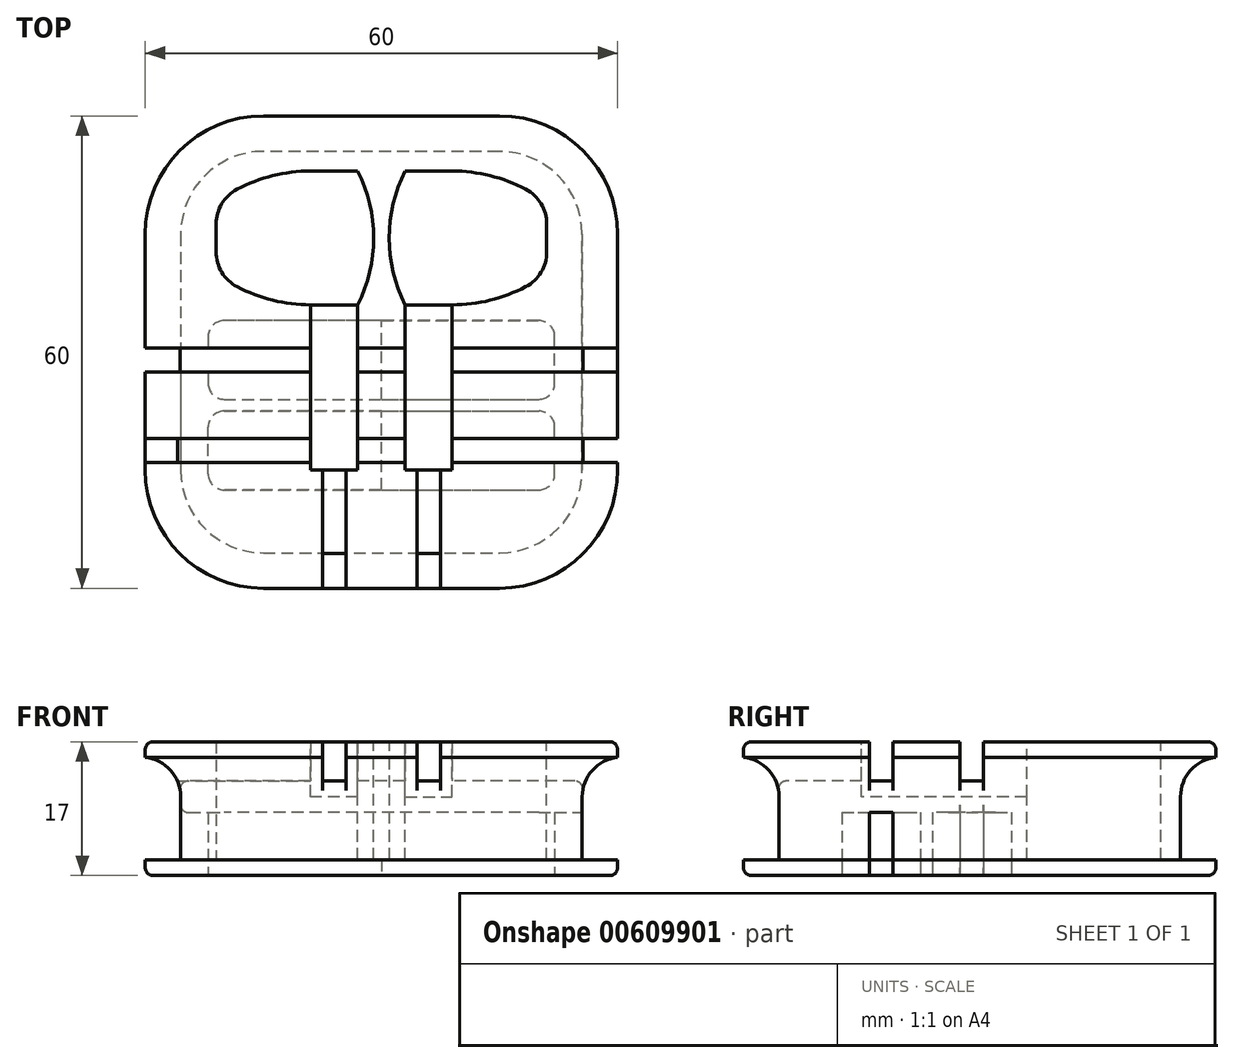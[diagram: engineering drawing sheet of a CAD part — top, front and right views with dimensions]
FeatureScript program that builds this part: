
annotation { "Feature Type Name" : "Feature", "Feature Type Description" : "" }
export const myFeature = defineFeature(function(context is Context, id is Id, definition is map)
    precondition{}
    {
        {
            var Q0;
            Q0=qCreatedBy(makeId("Top.planeOp"),FACE);
            var sketch = newSketch(context, id + "F0", { "sketchPlane" : qUnion([Q0])});
            skLineSegment(sketch, "E0.bottom", {"start": v(-30, 30) * mm, "end": v(30, 30) * mm});
            skLineSegment(sketch, "E0.top", {"start": v(-30, -30) * mm, "end": v(30, -30) * mm});
            skLineSegment(sketch, "E0.left", {"start": v(-30, 30) * mm, "end": v(-30, -30) * mm});
            skLineSegment(sketch, "E0.right", {"start": v(30, 30) * mm, "end": v(30, -30) * mm});
            skSolve(sketch);
        }
        {
            var Q0;
            Q0 = qSketchRegion(id + "F0", true);
            extrude(context, id + "F1", {"entities" : qUnion([Q0]), "endBound" : BoundingType.SYMMETRIC, "depth" : 17 * mm, "offsetDistance" : 25 * mm});
        }
        {
            var Q0;
            Q0=makeQuery(id+"F1.opExtrude","SWEPT_EDGE",EDGE,{"disambiguationData":[OSD([sQuery(id+"F0.wireOp",EDGE,"E0.bottom"),sQuery(id+"F0.wireOp",EDGE,"E0.left")])]});
            var Q1;
            Q1=makeQuery(id+"F1.opExtrude","SWEPT_EDGE",EDGE,{"disambiguationData":[OSD([sQuery(id+"F0.wireOp",EDGE,"E0.top"),sQuery(id+"F0.wireOp",EDGE,"E0.left")])]});
            var Q2;
            Q2=makeQuery(id+"F1.opExtrude","SWEPT_EDGE",EDGE,{"disambiguationData":[OSD([sQuery(id+"F0.wireOp",EDGE,"E0.bottom"),sQuery(id+"F0.wireOp",EDGE,"E0.right")])]});
            var Q3;
            Q3=makeQuery(id+"F1.opExtrude","SWEPT_EDGE",EDGE,{"disambiguationData":[OSD([sQuery(id+"F0.wireOp",EDGE,"E0.top"),sQuery(id+"F0.wireOp",EDGE,"E0.right")])]});
            fillet(context, id + "F2", {"entities" : qUnion([Q0, Q1, Q2, Q3]), "radius" : 15 * mm, "tangentPropagation" : true, "allowEdgeOverflow" : false});
        }
        {
            var Q0;
            Q0=makeQuery(id+"F1.opExtrude","CAP_FACE",FACE,{"disambiguationData":[OSD([sQuery(id+"F0.wireOp",EDGE,"E0.bottom"),sQuery(id+"F0.wireOp",EDGE,"E0.top"),sQuery(id+"F0.wireOp",EDGE,"E0.left"),sQuery(id+"F0.wireOp",EDGE,"E0.right")])],"isStart":false});
            cPlane(context, id + "F3", {"entities" : qUnion([Q0]), "cplaneType" : CPlaneType.OFFSET, "offset" : 2 * mm, "oppositeDirection" : true, "width" : 150 * mm, "height" : 150 * mm});
        }
        {
            var Q0;
            Q0=makeQuery(id+"F1.opExtrude","CAP_FACE",FACE,{"disambiguationData":[OSD([sQuery(id+"F0.wireOp",EDGE,"E0.bottom"),sQuery(id+"F0.wireOp",EDGE,"E0.top"),sQuery(id+"F0.wireOp",EDGE,"E0.left"),sQuery(id+"F0.wireOp",EDGE,"E0.right")])],"isStart":true});
            cPlane(context, id + "F4", {"entities" : qUnion([Q0]), "cplaneType" : CPlaneType.OFFSET, "offset" : 2 * mm, "oppositeDirection" : true, "width" : 150 * mm, "height" : 150 * mm});
        }
        {
            var Q0;
            Q0=qCreatedBy(id+"F3.planeOp",FACE);
            var sketch = newSketch(context, id + "F5", { "sketchPlane" : qUnion([Q0])});
            skLineSegment(sketch, "E1.0", {"start": v(-15, 25.5) * mm, "end": v(15, 25.5) * mm});
            skArc(sketch, "E1.1", {"start": v(25.5, 15) * mm, "mid": v(22.42, 22.42) * mm, "end": v(15, 25.5) * mm});
            skArc(sketch, "E1.2", {"start": v(-15, 25.5) * mm, "mid": v(-22.42, 22.42) * mm, "end": v(-25.5, 15) * mm});
            skLineSegment(sketch, "E1.3", {"start": v(25.5, 15) * mm, "end": v(25.5, -15) * mm});
            skLineSegment(sketch, "E1.4", {"start": v(-25.5, 15) * mm, "end": v(-25.5, -15) * mm});
            skArc(sketch, "E1.5", {"start": v(-25.5, -15) * mm, "mid": v(-22.42, -22.42) * mm, "end": v(-15, -25.5) * mm});
            skLineSegment(sketch, "E1.6", {"start": v(-15, -25.5) * mm, "end": v(15, -25.5) * mm});
            skArc(sketch, "E1.7", {"start": v(15, -25.5) * mm, "mid": v(22.42, -22.42) * mm, "end": v(25.5, -15) * mm});
            skLineSegment(sketch, "E2.0", {"start": v(-15, 30) * mm, "end": v(15, 30) * mm});
            skArc(sketch, "E3.0", {"start": v(-15, 30) * mm, "mid": v(-25.6, 25.6) * mm, "end": v(-30, 15) * mm});
            skLineSegment(sketch, "E4.0", {"start": v(-30, 15) * mm, "end": v(-30, -15) * mm});
            skArc(sketch, "E5.0", {"start": v(-30, -15) * mm, "mid": v(-25.6, -25.6) * mm, "end": v(-15, -30) * mm});
            skLineSegment(sketch, "E6.0", {"start": v(-15, -30) * mm, "end": v(15, -30) * mm});
            skArc(sketch, "E7.0", {"start": v(30, 15) * mm, "mid": v(25.6, 25.6) * mm, "end": v(15, 30) * mm});
            skLineSegment(sketch, "E8.0", {"start": v(30, 15) * mm, "end": v(30, -15) * mm});
            skArc(sketch, "E9.0", {"start": v(15, -30) * mm, "mid": v(25.6, -25.6) * mm, "end": v(30, -15) * mm});
            skSolve(sketch);
        }
        {
            var Q0;
            Q0 = qSketchRegion(id + "F5", true);
            var Q1;
            Q1=qCreatedBy(id+"F4.planeOp",FACE);
            extrude(context, id + "F6", {"entities" : qUnion([Q0]), "operationType" : NewBodyOperationType.REMOVE, "endBound" : BoundingType.UP_TO_SURFACE, "oppositeDirection" : true, "depth" : 25 * mm, "endBoundEntityFace" : qUnion([Q1]), "offsetDistance" : 25 * mm});
        }
        {
            var Q0;
            Q0=makeQuery(id+"F6.boolean.opBoolean","COPY",EDGE,{"derivedFrom":makeQuery(id+"F6.opExtrude","TWEAK_EDGE",EDGE,{"derivedFrom":[dummyQuery(id+"F4.planeOp",FACE),makeQuery(id+"F5.imprint","IMPRINT",EDGE,{"derivedFrom":sQuery(id+"F5.wireOp",EDGE,"E1.0")})]})});
            var Q1;
            Q1=makeQuery(id+"F6.boolean.opBoolean","COPY",EDGE,{"derivedFrom":makeQuery(id+"F6.opExtrude","CAP_EDGE",EDGE,{"disambiguationData":[OSD([sQuery(id+"F5.wireOp",EDGE,"E1.0")])],"isStart":true})});
            fillet(context, id + "F7", {"entities" : qUnion([Q0, Q1]), "radius" : 5 * mm, "tangentPropagation" : true, "allowEdgeOverflow" : false});
        }
        {
            var Q0;
            Q0=makeQuery(id+"F1.opExtrude","CAP_FACE",FACE,{"disambiguationData":[OSD([sQuery(id+"F0.wireOp",EDGE,"E0.bottom"),sQuery(id+"F0.wireOp",EDGE,"E0.top"),sQuery(id+"F0.wireOp",EDGE,"E0.left"),sQuery(id+"F0.wireOp",EDGE,"E0.right")])],"isStart":false});
            var sketch = newSketch(context, id + "F8", { "sketchPlane" : qUnion([Q0])});
            skLineSegment(sketch, "E10.bottom", {"start": v(3, 23) * mm, "end": v(9, 23) * mm});
            skLineSegment(sketch, "E10.top", {"start": v(3, -15) * mm, "end": v(9, -15) * mm});
            skLineSegment(sketch, "E10.left", {"start": v(3, 23) * mm, "end": v(3, -15) * mm});
            skLineSegment(sketch, "E10.right", {"start": v(9, 23) * mm, "end": v(9, -15) * mm});
            skLineSegment(sketch, "E11.MirrorCS", {"start": v(-9, 23) * mm, "end": v(-9, -15) * mm});
            skLineSegment(sketch, "E12.MirrorCS", {"start": v(-3, 23) * mm, "end": v(-3, -15) * mm});
            skLineSegment(sketch, "E13.MirrorCS", {"start": v(-3, -15) * mm, "end": v(-9, -15) * mm});
            skLineSegment(sketch, "E14.MirrorCS", {"start": v(-3, 23) * mm, "end": v(-9, 23) * mm});
            skSolve(sketch);
        }
        {
            var Q0;
            Q0 = qSketchRegion(id + "F8", true);
            extrude(context, id + "F9", {"entities" : qUnion([Q0]), "operationType" : NewBodyOperationType.REMOVE, "oppositeDirection" : true, "depth" : 7 * mm, "offsetDistance" : 25 * mm});
        }
        {
            var Q0;
            Q0=makeQuery(id+"F1.opExtrude","CAP_FACE",FACE,{"disambiguationData":[OSD([sQuery(id+"F0.wireOp",EDGE,"E0.bottom"),sQuery(id+"F0.wireOp",EDGE,"E0.top"),sQuery(id+"F0.wireOp",EDGE,"E0.left"),sQuery(id+"F0.wireOp",EDGE,"E0.right")])],"isStart":false});
            var sketch = newSketch(context, id + "F10", { "sketchPlane" : qUnion([Q0])});
            skLineSegment(sketch, "E15.0", {"start": v(3, 23) * mm, "end": v(9, 23) * mm});
            skLineSegment(sketch, "E16", {"start": v(3, 6) * mm, "end": v(9, 6) * mm});
            skArc(sketch, "E17", {"start": v(3, 23) * mm, "mid": v(1, 14.5) * mm, "end": v(3, 6) * mm});
            skLineSegment(sketch, "E18", {"start": v(21, 19) * mm, "end": v(21, 10) * mm});
            skArc(sketch, "E19", {"start": v(21, 19) * mm, "mid": v(15.32, 21.97) * mm, "end": v(9, 23) * mm});
            skArc(sketch, "E20", {"start": v(9, 6) * mm, "mid": v(15.32, 7.03) * mm, "end": v(21, 10) * mm});
            skLineSegment(sketch, "E21.MirrorCS", {"start": v(-21, 19) * mm, "end": v(-21, 10) * mm});
            skArc(sketch, "E22.MirrorCS", {"start": v(-9, 6) * mm, "mid": v(-15.32, 7.03) * mm, "end": v(-21, 10) * mm});
            skArc(sketch, "E23.MirrorCS", {"start": v(-21, 19) * mm, "mid": v(-15.32, 21.97) * mm, "end": v(-9, 23) * mm});
            skArc(sketch, "E24.MirrorCS", {"start": v(-3, 23) * mm, "mid": v(-1, 14.5) * mm, "end": v(-3, 6) * mm});
            skLineSegment(sketch, "E25.MirrorCS", {"start": v(-3, 23) * mm, "end": v(-9, 23) * mm});
            skLineSegment(sketch, "E26.MirrorCS", {"start": v(-3, 6) * mm, "end": v(-9, 6) * mm});
            skSolve(sketch);
        }
        {
            var Q0;
            Q0 = qSketchRegion(id + "F10", true);
            var Q1;
            Q1=qCreatedBy(id+"F4.planeOp",FACE);
            extrude(context, id + "F11", {"entities" : qUnion([Q0]), "operationType" : NewBodyOperationType.REMOVE, "endBound" : BoundingType.UP_TO_SURFACE, "oppositeDirection" : true, "depth" : 18 * mm, "endBoundEntityFace" : qUnion([Q1]), "offsetDistance" : 25 * mm});
        }
        {
            var Q0;
            Q0=makeQuery(id+"F1.opExtrude","CAP_FACE",FACE,{"disambiguationData":[OSD([sQuery(id+"F0.wireOp",EDGE,"E0.bottom"),sQuery(id+"F0.wireOp",EDGE,"E0.top"),sQuery(id+"F0.wireOp",EDGE,"E0.left"),sQuery(id+"F0.wireOp",EDGE,"E0.right")])],"isStart":false});
            var sketch = newSketch(context, id + "F12", { "sketchPlane" : qUnion([Q0])});
            skLineSegment(sketch, "E27.0", {"start": v(-7.5, -30) * mm, "end": v(-4.5, -30) * mm});
            skLineSegment(sketch, "E28.0", {"start": v(-4.5, -15) * mm, "end": v(-7.5, -15) * mm});
            skLineSegment(sketch, "E29", {"start": v(-6, -15) * mm, "end": v(-6, -30) * mm, "construction": true});
            skLineSegment(sketch, "E30", {"start": v(-7.5, -15) * mm, "end": v(-7.5, -30) * mm});
            skLineSegment(sketch, "E31", {"start": v(-4.5, -15) * mm, "end": v(-4.5, -30) * mm});
            skPoint(sketch, "E32.orphan", {"position": v(-3, -15) * mm});
            skPoint(sketch, "E33.orphan", {"position": v(-9, -15) * mm});
            skPoint(sketch, "E34.orphan", {"position": v(-15, -30) * mm});
            skLineSegment(sketch, "E35.MirrorCS", {"start": v(7.5, -30) * mm, "end": v(4.5, -30) * mm});
            skLineSegment(sketch, "E36.MirrorCS", {"start": v(4.5, -15) * mm, "end": v(7.5, -15) * mm});
            skPoint(sketch, "E37.MirrorP", {"position": v(9, -15) * mm});
            skPoint(sketch, "E38.MirrorP", {"position": v(3, -15) * mm});
            skLineSegment(sketch, "E39.MirrorCS", {"start": v(6, -15) * mm, "end": v(6, -30) * mm, "construction": true});
            skLineSegment(sketch, "E40.MirrorCS", {"start": v(7.5, -15) * mm, "end": v(7.5, -30) * mm});
            skLineSegment(sketch, "E41.MirrorCS", {"start": v(4.5, -15) * mm, "end": v(4.5, -30) * mm});
            skLineSegment(sketch, "E42.top", {"start": v(30, -2.5) * mm, "end": v(-30, -2.5) * mm});
            skLineSegment(sketch, "E42.left", {"start": v(30, 0.5) * mm, "end": v(30, -2.5) * mm});
            skLineSegment(sketch, "E42.right", {"start": v(-30, 0.5) * mm, "end": v(-30, -2.5) * mm});
            skLineSegment(sketch, "E43", {"start": v(-30, 0.5) * mm, "end": v(30, 0.5) * mm});
            skPoint(sketch, "E44.orphan", {"position": v(30, 0) * mm});
            skSolve(sketch);
        }
        {
            var Q0;
            Q0 = qSketchRegion(id + "F12", true);
            extrude(context, id + "F13", {"entities" : qUnion([Q0]), "operationType" : NewBodyOperationType.REMOVE, "oppositeDirection" : true, "depth" : 5 * mm, "offsetDistance" : 25 * mm});
        }
        {
            var Q0;
            Q0=makeQuery(id+"F1.opExtrude","CAP_FACE",FACE,{"disambiguationData":[OSD([sQuery(id+"F0.wireOp",EDGE,"E0.bottom"),sQuery(id+"F0.wireOp",EDGE,"E0.top"),sQuery(id+"F0.wireOp",EDGE,"E0.left"),sQuery(id+"F0.wireOp",EDGE,"E0.right")])],"isStart":true});
            var sketch = newSketch(context, id + "F14", { "sketchPlane" : qUnion([Q0])});
            skLineSegment(sketch, "E45.bottom", {"start": v(-30, -0.5) * mm, "end": v(-22, -0.5) * mm});
            skLineSegment(sketch, "E45.top", {"start": v(-30, 2.5) * mm, "end": v(-22, 2.5) * mm});
            skLineSegment(sketch, "E45.left", {"start": v(-30, -0.5) * mm, "end": v(-30, 2.5) * mm});
            skLineSegment(sketch, "E46", {"start": v(-30, 1) * mm, "end": v(30, 1) * mm, "construction": true});
            skLineSegment(sketch, "E47", {"start": v(-22, 2.5) * mm, "end": v(-22, 6) * mm});
            skLineSegment(sketch, "E48", {"start": v(-22, 6) * mm, "end": v(0, 6) * mm});
            skLineSegment(sketch, "E49", {"start": v(0, 6) * mm, "end": v(0, -4) * mm});
            skLineSegment(sketch, "E50", {"start": v(0, -4) * mm, "end": v(-22, -4) * mm});
            skLineSegment(sketch, "E51", {"start": v(-22, -4) * mm, "end": v(-22, -0.5) * mm});
            skLineSegment(sketch, "E52.bottom", {"start": v(0, 17.5) * mm, "end": v(22, 17.5) * mm});
            skLineSegment(sketch, "E52.top", {"start": v(0, 7.5) * mm, "end": v(22, 7.5) * mm});
            skLineSegment(sketch, "E52.left", {"start": v(0, 17.5) * mm, "end": v(0, 7.5) * mm});
            skLineSegment(sketch, "E52.right", {"start": v(22, 17.5) * mm, "end": v(22, 14) * mm});
            skLineSegment(sketch, "E53", {"start": v(0, 12.5) * mm, "end": v(29.8, 12.5) * mm, "construction": true});
            skPoint(sketch, "E54.orphan", {"position": v(15, 30) * mm});
            skPoint(sketch, "E55.orphan", {"position": v(30, 15) * mm});
            skLineSegment(sketch, "E56.trimOffspring", {"start": v(22, 11) * mm, "end": v(22, 7.5) * mm});
            skLineSegment(sketch, "E57", {"start": v(22, 11) * mm, "end": v(30, 11) * mm});
            skLineSegment(sketch, "E58", {"start": v(22, 14) * mm, "end": v(30, 14) * mm});
            skLineSegment(sketch, "E59.trimOffspring", {"start": v(30, 11) * mm, "end": v(30, 14) * mm});
            skSolve(sketch);
        }
        {
            var Q0;
            Q0 = qSketchRegion(id + "F14", true);
            extrude(context, id + "F15", {"entities" : qUnion([Q0]), "operationType" : NewBodyOperationType.REMOVE, "oppositeDirection" : true, "depth" : 8 * mm, "offsetDistance" : 25 * mm});
        }
        {
            var Q0;
            Q0=qCreatedBy(id+"F4.planeOp",FACE);
            var sketch = newSketch(context, id + "F16", { "sketchPlane" : qUnion([Q0])});
            skPoint(sketch, "E60.0", {"position": v(0, 6) * mm});
            skPoint(sketch, "E61.0", {"position": v(0, -4) * mm});
            skLineSegment(sketch, "E62.bottom", {"start": v(0, 6) * mm, "end": v(22, 6) * mm});
            skLineSegment(sketch, "E62.top", {"start": v(0, -4) * mm, "end": v(22, -4) * mm});
            skLineSegment(sketch, "E62.left", {"start": v(0, 6) * mm, "end": v(0, -4) * mm});
            skLineSegment(sketch, "E62.right", {"start": v(22, 6) * mm, "end": v(22, -4) * mm});
            skPoint(sketch, "E63.0", {"position": v(0, 17.5) * mm});
            skPoint(sketch, "E64.0", {"position": v(0, 7.5) * mm});
            skLineSegment(sketch, "E65.bottom", {"start": v(0, 17.5) * mm, "end": v(-22, 17.5) * mm});
            skLineSegment(sketch, "E65.top", {"start": v(0, 7.5) * mm, "end": v(-22, 7.5) * mm});
            skLineSegment(sketch, "E65.left", {"start": v(0, 17.5) * mm, "end": v(0, 7.5) * mm});
            skLineSegment(sketch, "E65.right", {"start": v(-22, 17.5) * mm, "end": v(-22, 7.5) * mm});
            skSolve(sketch);
        }
        {
            var Q0;
            Q0 = qSketchRegion(id + "F16", true);
            extrude(context, id + "F17", {"entities" : qUnion([Q0]), "operationType" : NewBodyOperationType.REMOVE, "oppositeDirection" : true, "depth" : 6 * mm, "offsetDistance" : 25 * mm});
        }
        {
            var Q0;
            {var subQ0=sQuery(id+"F0.wireOp",EDGE,"E0.left");var subQ1=sQuery(id+"F0.wireOp",EDGE,"E0.top");Q0=makeQuery(id+"F13.boolean.opBoolean","SPLIT",FACE,{"disambiguationData":[TD([makeQuery(id+"F13.opExtrude","SWEPT_FACE",FACE,{"disambiguationData":[OSD([sQuery(id+"F12.wireOp",EDGE,"E30")])]})])],"derivedFrom":makeQuery(id+"F1.opExtrude","CAP_FACE",FACE,{"disambiguationData":[OSD([sQuery(id+"F0.wireOp",EDGE,"E0.bottom"),subQ1,subQ0,sQuery(id+"F0.wireOp",EDGE,"E0.right")])],"isStart":false})});}
            var sketch = newSketch(context, id + "F18", { "sketchPlane" : qUnion([Q0])});
            skPoint(sketch, "E66.orphan", {"position": v(30, -15) * mm});
            skPoint(sketch, "E67.orphan", {"position": v(15, -30) * mm});
            skPoint(sketch, "E68.orphan", {"position": v(-15, -30) * mm});
            skPoint(sketch, "E69.orphan", {"position": v(-30, -15) * mm});
            skPoint(sketch, "E70.0", {"position": v(30, -11) * mm});
            skPoint(sketch, "E71.0", {"position": v(30, -14) * mm});
            skLineSegment(sketch, "E72", {"start": v(30, -11) * mm, "end": v(-30, -11) * mm});
            skLineSegment(sketch, "E73", {"start": v(30, -14) * mm, "end": v(-30, -14) * mm});
            skLineSegment(sketch, "E74", {"start": v(-30, -14) * mm, "end": v(-30, -11) * mm});
            skLineSegment(sketch, "E75", {"start": v(30, -11) * mm, "end": v(30, -14) * mm});
            skSolve(sketch);
        }
        {
            var Q0;
            Q0 = qSketchRegion(id + "F18", true);
            var Q1;
            {var subQ0=sQuery(id+"F12.wireOp",EDGE,"E42.top");var subQ1=sQuery(id+"F12.wireOp",EDGE,"E43");Q1=makeQuery(id+"F13.boolean.opBoolean","COPY",FACE,{"disambiguationData":[TD([makeQuery(id+"F7.opFillet","BLEND_FACE",FACE,{"disambiguationData":[OSD([sQuery(id+"F5.wireOp",EDGE,"E1.3")])]})])],"derivedFrom":makeQuery(id+"F13.opExtrude","CAP_FACE",FACE,{"disambiguationData":[OSD([subQ0,sQuery(id+"F12.wireOp",EDGE,"E42.left"),sQuery(id+"F12.wireOp",EDGE,"E42.right"),subQ1])],"isStart":false})});}
            extrude(context, id + "F19", {"entities" : qUnion([Q0]), "operationType" : NewBodyOperationType.REMOVE, "endBound" : BoundingType.UP_TO_SURFACE, "oppositeDirection" : true, "depth" : 25 * mm, "endBoundEntityFace" : qUnion([Q1]), "offsetDistance" : 25 * mm});
        }
        {
            var Q0;
            Q0=makeQuery(id+"F13.boolean.opBoolean","INTERSECT",EDGE,{"derivedFrom":[makeQuery(id+"F7.opFillet","BLEND_FACE",FACE,{"disambiguationData":[OSD([sQuery(id+"F5.wireOp",EDGE,"E1.6")])]}),makeQuery(id+"F13.opExtrude","CAP_FACE",FACE,{"disambiguationData":[OSD([sQuery(id+"F12.wireOp",EDGE,"E27.0"),sQuery(id+"F12.wireOp",EDGE,"E28.0"),sQuery(id+"F12.wireOp",EDGE,"E30"),sQuery(id+"F12.wireOp",EDGE,"E31")])],"isStart":false})]});
            var Q1;
            Q1=makeQuery(id+"F13.boolean.opBoolean","INTERSECT",EDGE,{"derivedFrom":[makeQuery(id+"F7.opFillet","BLEND_FACE",FACE,{"disambiguationData":[OSD([sQuery(id+"F5.wireOp",EDGE,"E1.6")])]}),makeQuery(id+"F13.opExtrude","CAP_FACE",FACE,{"disambiguationData":[OSD([sQuery(id+"F12.wireOp",EDGE,"E35.MirrorCS"),sQuery(id+"F12.wireOp",EDGE,"E36.MirrorCS"),sQuery(id+"F12.wireOp",EDGE,"E40.MirrorCS"),sQuery(id+"F12.wireOp",EDGE,"E41.MirrorCS")])],"isStart":false})]});
            var Q2;
            Q2=makeQuery(id+"F13.boolean.opBoolean","INTERSECT",EDGE,{"derivedFrom":[makeQuery(id+"F7.opFillet","BLEND_FACE",FACE,{"disambiguationData":[OSD([sQuery(id+"F5.wireOp",EDGE,"E1.3")])]}),makeQuery(id+"F13.opExtrude","CAP_FACE",FACE,{"disambiguationData":[OSD([sQuery(id+"F12.wireOp",EDGE,"E42.top"),sQuery(id+"F12.wireOp",EDGE,"E42.left"),sQuery(id+"F12.wireOp",EDGE,"E42.right"),sQuery(id+"F12.wireOp",EDGE,"E43")])],"isStart":false})]});
            var Q3;
            Q3=makeQuery(id+"F15.boolean.opBoolean","INTERSECT",EDGE,{"derivedFrom":[makeQuery(id+"F6.boolean.opBoolean","COPY",FACE,{"derivedFrom":makeQuery(id+"F6.opExtrude","SWEPT_FACE",FACE,{"disambiguationData":[OSD([sQuery(id+"F5.wireOp",EDGE,"E1.4")])]})}),makeQuery(id+"F15.opExtrude","CAP_FACE",FACE,{"disambiguationData":[OSD([sQuery(id+"F14.wireOp",EDGE,"E45.bottom"),sQuery(id+"F14.wireOp",EDGE,"E45.top"),sQuery(id+"F14.wireOp",EDGE,"E45.left"),sQuery(id+"F14.wireOp",EDGE,"E47"),sQuery(id+"F14.wireOp",EDGE,"E48"),sQuery(id+"F14.wireOp",EDGE,"E49"),sQuery(id+"F14.wireOp",EDGE,"E50"),sQuery(id+"F14.wireOp",EDGE,"E51")])],"isStart":false})]});
            var Q4;
            Q4=makeQuery(id+"F13.boolean.opBoolean","INTERSECT",EDGE,{"derivedFrom":[makeQuery(id+"F7.opFillet","BLEND_FACE",FACE,{"disambiguationData":[OSD([sQuery(id+"F5.wireOp",EDGE,"E1.4")])]}),makeQuery(id+"F13.opExtrude","CAP_FACE",FACE,{"disambiguationData":[OSD([sQuery(id+"F12.wireOp",EDGE,"E42.top"),sQuery(id+"F12.wireOp",EDGE,"E42.left"),sQuery(id+"F12.wireOp",EDGE,"E42.right"),sQuery(id+"F12.wireOp",EDGE,"E43")])],"isStart":false})]});
            var Q5;
            Q5=makeQuery(id+"F15.boolean.opBoolean","INTERSECT",EDGE,{"derivedFrom":[makeQuery(id+"F6.boolean.opBoolean","COPY",FACE,{"derivedFrom":makeQuery(id+"F6.opExtrude","SWEPT_FACE",FACE,{"disambiguationData":[OSD([sQuery(id+"F5.wireOp",EDGE,"E1.7")])]})}),makeQuery(id+"F15.opExtrude","CAP_FACE",FACE,{"disambiguationData":[OSD([sQuery(id+"F14.wireOp",EDGE,"E52.bottom"),sQuery(id+"F14.wireOp",EDGE,"E52.top"),sQuery(id+"F14.wireOp",EDGE,"E52.left"),sQuery(id+"F14.wireOp",EDGE,"E52.right"),sQuery(id+"F14.wireOp",EDGE,"f2b6bd09-745d-466a-85ff-806cd32a10e5.0"),sQuery(id+"F14.wireOp",EDGE,"2cRdxzpE-s3Wx-fRDt-1MXC-Jum1L93l91ge"),sQuery(id+"F14.wireOp",EDGE,"9VPsuItm-Mm5I-2wE3-i7sN-2tQMlh2Qrenv"),sQuery(id+"F14.wireOp",EDGE,"E56.trimOffspring")])],"isStart":false})]});
            var Q6;
            Q6=makeQuery(id+"F19.boolean.opBoolean","INTERSECT",EDGE,{"derivedFrom":[makeQuery(id+"F7.opFillet","BLEND_FACE",FACE,{"disambiguationData":[OSD([sQuery(id+"F5.wireOp",EDGE,"E1.3")])]}),makeQuery(id+"F19.opExtrude","CAP_FACE",FACE,{"disambiguationData":[OSD([sQuery(id+"F18.wireOp",EDGE,"E72"),sQuery(id+"F18.wireOp",EDGE,"E73"),sQuery(id+"F18.wireOp",EDGE,"E74"),sQuery(id+"F18.wireOp",EDGE,"E75")])],"isStart":false})]});
            fillet(context, id + "F20", {"entities" : qUnion([Q0, Q1, Q2, Q3, Q4, Q5, Q6]), "radius" : 1 * mm, "tangentPropagation" : true, "allowEdgeOverflow" : false});
        }
        {
            var Q0;
            {var subQ0=sQuery(id+"F0.wireOp",EDGE,"E0.right");var subQ1=sQuery(id+"F0.wireOp",EDGE,"E0.top");Q0=makeQuery(id+"F2.opFillet","BLEND_EDGE",EDGE,{"blendedFrom":[makeQuery(id+"F1.opExtrude","SWEPT_EDGE",EDGE,{"disambiguationData":[OSD([subQ1,subQ0])]}),makeQuery(id+"F1.opExtrude","CAP_FACE",FACE,{"disambiguationData":[OSD([sQuery(id+"F0.wireOp",EDGE,"E0.bottom"),subQ1,sQuery(id+"F0.wireOp",EDGE,"E0.left"),subQ0])],"isStart":false})],"blendedInto":[makeQuery(id+"F1.opExtrude","CAP_FACE",FACE,{"disambiguationData":[OSD([sQuery(id+"F0.wireOp",EDGE,"E0.bottom"),subQ1,sQuery(id+"F0.wireOp",EDGE,"E0.left"),subQ0])],"isStart":false})]});}
            var Q1;
            {var subQ0=sQuery(id+"F0.wireOp",EDGE,"E0.top");Q1=makeQuery(id+"F13.boolean.opBoolean","SPLIT",EDGE,{"disambiguationData":[TD([makeQuery(id+"F13.opExtrude","SWEPT_FACE",FACE,{"disambiguationData":[OSD([sQuery(id+"F12.wireOp",EDGE,"E31")])]})])],"derivedFrom":makeQuery(id+"F1.opExtrude","CAP_EDGE",EDGE,{"disambiguationData":[OSD([subQ0])],"isStart":false})});}
            var Q2;
            {var subQ0=sQuery(id+"F0.wireOp",EDGE,"E0.left");var subQ1=sQuery(id+"F0.wireOp",EDGE,"E0.top");Q2=makeQuery(id+"F2.opFillet","BLEND_EDGE",EDGE,{"blendedFrom":[makeQuery(id+"F1.opExtrude","SWEPT_EDGE",EDGE,{"disambiguationData":[OSD([subQ1,subQ0])]}),makeQuery(id+"F1.opExtrude","CAP_FACE",FACE,{"disambiguationData":[OSD([sQuery(id+"F0.wireOp",EDGE,"E0.bottom"),subQ1,subQ0,sQuery(id+"F0.wireOp",EDGE,"E0.right")])],"isStart":false})],"blendedInto":[makeQuery(id+"F1.opExtrude","CAP_FACE",FACE,{"disambiguationData":[OSD([sQuery(id+"F0.wireOp",EDGE,"E0.bottom"),subQ1,subQ0,sQuery(id+"F0.wireOp",EDGE,"E0.right")])],"isStart":false})]});}
            var Q3;
            {var subQ0=sQuery(id+"F0.wireOp",EDGE,"E0.left");Q3=makeQuery(id+"F13.boolean.opBoolean","SPLIT",EDGE,{"disambiguationData":[TD([makeQuery(id+"F13.opExtrude","SWEPT_FACE",FACE,{"disambiguationData":[OSD([sQuery(id+"F12.wireOp",EDGE,"E43")])]})])],"derivedFrom":makeQuery(id+"F1.opExtrude","CAP_EDGE",EDGE,{"disambiguationData":[OSD([subQ0])],"isStart":false})});}
            var Q4;
            {var subQ0=sQuery(id+"F0.wireOp",EDGE,"E0.right");var subQ1=sQuery(id+"F0.wireOp",EDGE,"E0.bottom");Q4=makeQuery(id+"F2.opFillet","BLEND_EDGE",EDGE,{"blendedFrom":[makeQuery(id+"F1.opExtrude","SWEPT_EDGE",EDGE,{"disambiguationData":[OSD([subQ1,subQ0])]}),makeQuery(id+"F1.opExtrude","CAP_FACE",FACE,{"disambiguationData":[OSD([subQ1,sQuery(id+"F0.wireOp",EDGE,"E0.top"),sQuery(id+"F0.wireOp",EDGE,"E0.left"),subQ0])],"isStart":false})],"blendedInto":[makeQuery(id+"F1.opExtrude","CAP_FACE",FACE,{"disambiguationData":[OSD([subQ1,sQuery(id+"F0.wireOp",EDGE,"E0.top"),sQuery(id+"F0.wireOp",EDGE,"E0.left"),subQ0])],"isStart":false})]});}
            var Q5;
            {var subQ0=sQuery(id+"F0.wireOp",EDGE,"E0.right");var subQ1=sQuery(id+"F0.wireOp",EDGE,"E0.top");Q5=makeQuery(id+"F2.opFillet","BLEND_EDGE",EDGE,{"blendedFrom":[makeQuery(id+"F1.opExtrude","SWEPT_EDGE",EDGE,{"disambiguationData":[OSD([subQ1,subQ0])]}),makeQuery(id+"F1.opExtrude","CAP_FACE",FACE,{"disambiguationData":[OSD([sQuery(id+"F0.wireOp",EDGE,"E0.bottom"),subQ1,sQuery(id+"F0.wireOp",EDGE,"E0.left"),subQ0])],"isStart":true})],"blendedInto":[makeQuery(id+"F1.opExtrude","CAP_FACE",FACE,{"disambiguationData":[OSD([sQuery(id+"F0.wireOp",EDGE,"E0.bottom"),subQ1,sQuery(id+"F0.wireOp",EDGE,"E0.left"),subQ0])],"isStart":true})]});}
            var Q6;
            Q6=makeQuery(id+"F1.opExtrude","CAP_EDGE",EDGE,{"disambiguationData":[OSD([sQuery(id+"F0.wireOp",EDGE,"E0.top")])],"isStart":true});
            var Q7;
            {var subQ0=sQuery(id+"F0.wireOp",EDGE,"E0.right");Q7=makeQuery(id+"F15.boolean.opBoolean","SPLIT",EDGE,{"disambiguationData":[TD([makeQuery(id+"F15.opExtrude","SWEPT_FACE",FACE,{"disambiguationData":[OSD([sQuery(id+"F14.wireOp",EDGE,"E57")])]})])],"derivedFrom":makeQuery(id+"F1.opExtrude","CAP_EDGE",EDGE,{"disambiguationData":[OSD([subQ0])],"isStart":true})});}
            var Q8;
            {var subQ0=sQuery(id+"F0.wireOp",EDGE,"E0.right");var subQ4=sQuery(id+"F12.wireOp",EDGE,"E42.top");var subQ5=makeQuery(id+"F13.opExtrude","SWEPT_FACE",FACE,{"disambiguationData":[OSD([subQ4])]});Q8=makeQuery(id+"F19.boolean.opBoolean","SPLIT",EDGE,{"disambiguationData":[TD([makeQuery(id+"F19.opExtrude","SWEPT_FACE",FACE,{"disambiguationData":[OSD([sQuery(id+"F18.wireOp",EDGE,"E72")])]})])],"derivedFrom":makeQuery(id+"F13.boolean.opBoolean","SPLIT",EDGE,{"disambiguationData":[TD([subQ5])],"derivedFrom":makeQuery(id+"F1.opExtrude","CAP_EDGE",EDGE,{"disambiguationData":[OSD([subQ0])],"isStart":false})})});}
            var Q9;
            {var subQ0=sQuery(id+"F0.wireOp",EDGE,"E0.left");var subQ4=sQuery(id+"F12.wireOp",EDGE,"E42.top");var subQ5=makeQuery(id+"F13.opExtrude","SWEPT_FACE",FACE,{"disambiguationData":[OSD([subQ4])]});Q9=makeQuery(id+"F19.boolean.opBoolean","SPLIT",EDGE,{"disambiguationData":[TD([makeQuery(id+"F19.opExtrude","SWEPT_FACE",FACE,{"disambiguationData":[OSD([sQuery(id+"F18.wireOp",EDGE,"E72")])]})])],"derivedFrom":makeQuery(id+"F13.boolean.opBoolean","SPLIT",EDGE,{"disambiguationData":[TD([subQ5])],"derivedFrom":makeQuery(id+"F1.opExtrude","CAP_EDGE",EDGE,{"disambiguationData":[OSD([subQ0])],"isStart":false})})});}
            fillet(context, id + "F21", {"entities" : qUnion([Q0, Q1, Q2, Q3, Q4, Q5, Q6, Q7, Q8, Q9]), "radius" : 1 * mm, "tangentPropagation" : true, "allowEdgeOverflow" : false});
        }
        {
            var Q0;
            Q0=makeQuery(id+"F11.boolean.opBoolean","COPY",EDGE,{"derivedFrom":makeQuery(id+"F11.opExtrude","SWEPT_EDGE",EDGE,{"disambiguationData":[OSD([sQuery(id+"F10.wireOp",EDGE,"E18"),sQuery(id+"F10.wireOp",EDGE,"E19")])]})});
            var Q1;
            Q1=makeQuery(id+"F11.boolean.opBoolean","COPY",EDGE,{"derivedFrom":makeQuery(id+"F11.opExtrude","SWEPT_EDGE",EDGE,{"disambiguationData":[OSD([sQuery(id+"F10.wireOp",EDGE,"E18"),sQuery(id+"F10.wireOp",EDGE,"E20")])]})});
            var Q2;
            Q2=makeQuery(id+"F11.boolean.opBoolean","COPY",EDGE,{"derivedFrom":makeQuery(id+"F11.opExtrude","SWEPT_EDGE",EDGE,{"disambiguationData":[OSD([sQuery(id+"F10.wireOp",EDGE,"E21.MirrorCS"),sQuery(id+"F10.wireOp",EDGE,"E23.MirrorCS")])]})});
            var Q3;
            Q3=makeQuery(id+"F11.boolean.opBoolean","COPY",EDGE,{"derivedFrom":makeQuery(id+"F11.opExtrude","SWEPT_EDGE",EDGE,{"disambiguationData":[OSD([sQuery(id+"F10.wireOp",EDGE,"E21.MirrorCS"),sQuery(id+"F10.wireOp",EDGE,"E22.MirrorCS")])]})});
            fillet(context, id + "F22", {"entities" : qUnion([Q0, Q1, Q2, Q3]), "radius" : 5 * mm, "tangentPropagation" : true, "allowEdgeOverflow" : false});
        }
        {
            var Q0;
            Q0=makeQuery(id+"F15.boolean.opBoolean","COPY",EDGE,{"derivedFrom":makeQuery(id+"F15.opExtrude","SWEPT_EDGE",EDGE,{"disambiguationData":[OSD([sQuery(id+"F14.wireOp",EDGE,"E52.top"),sQuery(id+"F14.wireOp",EDGE,"E56.trimOffspring")])]})});
            var Q1;
            Q1=makeQuery(id+"F15.boolean.opBoolean","COPY",EDGE,{"derivedFrom":makeQuery(id+"F15.opExtrude","SWEPT_EDGE",EDGE,{"disambiguationData":[OSD([sQuery(id+"F14.wireOp",EDGE,"E52.bottom"),sQuery(id+"F14.wireOp",EDGE,"E52.right")])]})});
            var Q2;
            Q2=makeQuery(id+"F17.boolean.opBoolean","COPY",EDGE,{"derivedFrom":makeQuery(id+"F17.opExtrude","SWEPT_EDGE",EDGE,{"disambiguationData":[OSD([sQuery(id+"F16.wireOp",EDGE,"E62.top"),sQuery(id+"F16.wireOp",EDGE,"E62.right")])]})});
            var Q3;
            Q3=makeQuery(id+"F17.boolean.opBoolean","COPY",EDGE,{"derivedFrom":makeQuery(id+"F17.opExtrude","SWEPT_EDGE",EDGE,{"disambiguationData":[OSD([sQuery(id+"F16.wireOp",EDGE,"E62.bottom"),sQuery(id+"F16.wireOp",EDGE,"E62.right")])]})});
            var Q4;
            Q4=makeQuery(id+"F17.boolean.opBoolean","COPY",EDGE,{"derivedFrom":makeQuery(id+"F17.opExtrude","SWEPT_EDGE",EDGE,{"disambiguationData":[OSD([sQuery(id+"F16.wireOp",EDGE,"E65.top"),sQuery(id+"F16.wireOp",EDGE,"E65.right")])]})});
            var Q5;
            Q5=makeQuery(id+"F17.boolean.opBoolean","COPY",EDGE,{"derivedFrom":makeQuery(id+"F17.opExtrude","SWEPT_EDGE",EDGE,{"disambiguationData":[OSD([sQuery(id+"F16.wireOp",EDGE,"E65.bottom"),sQuery(id+"F16.wireOp",EDGE,"E65.right")])]})});
            var Q6;
            Q6=makeQuery(id+"F15.boolean.opBoolean","COPY",EDGE,{"derivedFrom":makeQuery(id+"F15.opExtrude","SWEPT_EDGE",EDGE,{"disambiguationData":[OSD([sQuery(id+"F14.wireOp",EDGE,"E47"),sQuery(id+"F14.wireOp",EDGE,"E48")])]})});
            var Q7;
            Q7=makeQuery(id+"F15.boolean.opBoolean","COPY",EDGE,{"derivedFrom":makeQuery(id+"F15.opExtrude","SWEPT_EDGE",EDGE,{"disambiguationData":[OSD([sQuery(id+"F14.wireOp",EDGE,"E50"),sQuery(id+"F14.wireOp",EDGE,"E51")])]})});
            fillet(context, id + "F23", {"entities" : qUnion([Q0, Q1, Q2, Q3, Q4, Q5, Q6, Q7]), "radius" : 2 * mm, "tangentPropagation" : true, "allowEdgeOverflow" : false});
        }
    });
